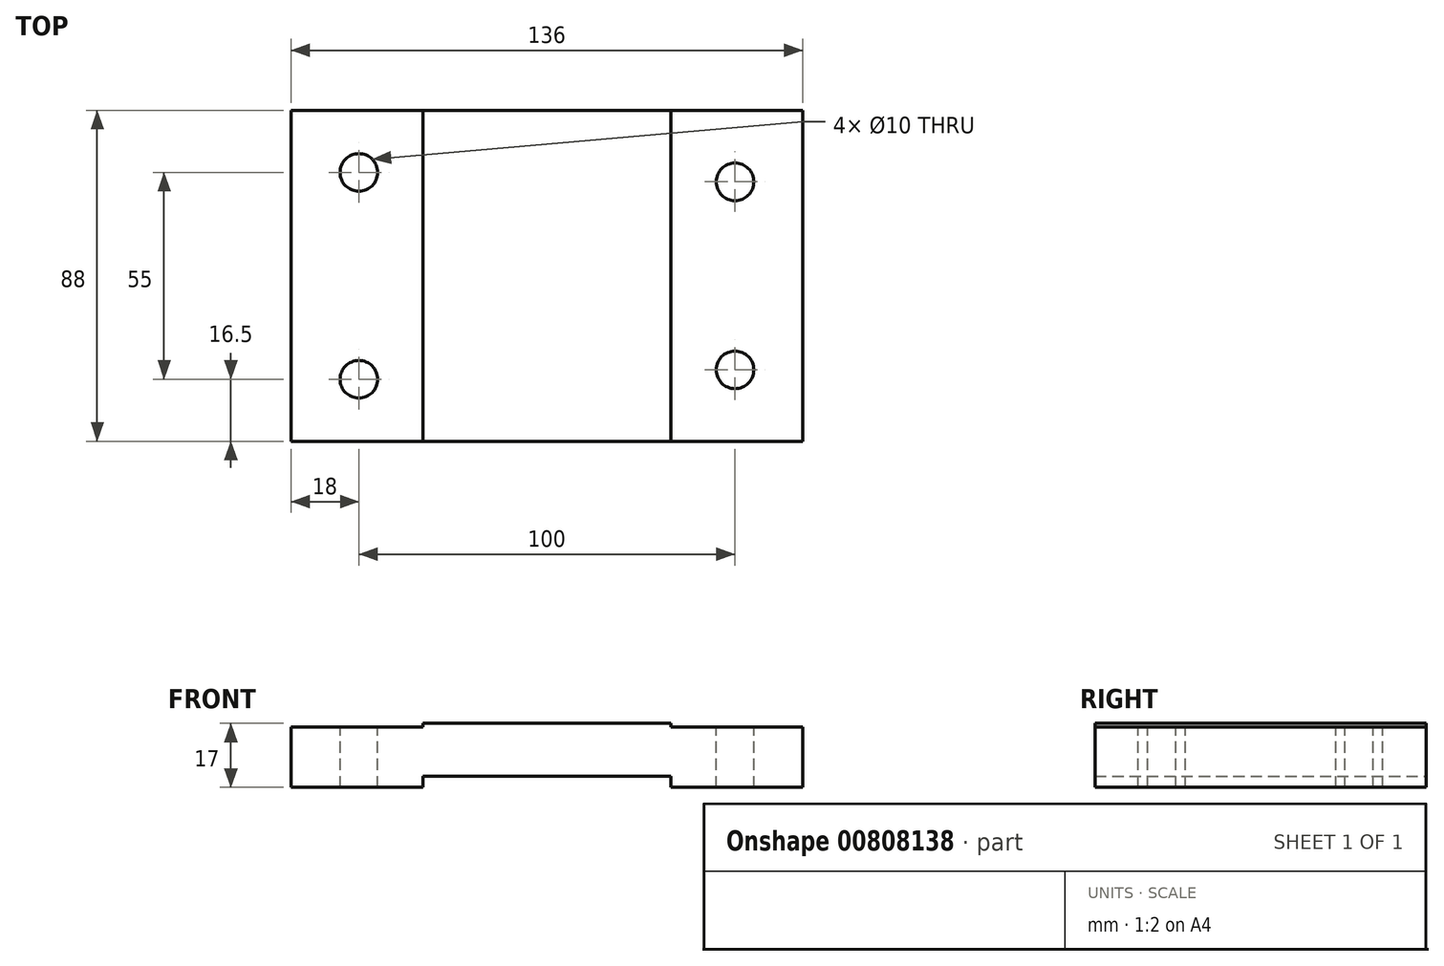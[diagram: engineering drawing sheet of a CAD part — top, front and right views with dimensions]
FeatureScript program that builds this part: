
annotation { "Feature Type Name" : "Feature", "Feature Type Description" : "" }
export const myFeature = defineFeature(function(context is Context, id is Id, definition is map)
    precondition{}
    {
        {
            var Q0;
            Q0=qCreatedBy(makeId("Front.planeOp"),FACE);
            var sketch = newSketch(context, id + "F0", { "sketchPlane" : qUnion([Q0])});
            skLineSegment(sketch, "E0.bottom", {"start": v(-33, 0) * mm, "end": v(-68, 0) * mm});
            skLineSegment(sketch, "E0.top", {"start": v(-33, 16) * mm, "end": v(-68, 16) * mm});
            skLineSegment(sketch, "E0.left", {"start": v(-33, 0) * mm, "end": v(-33, 16) * mm});
            skLineSegment(sketch, "E0.right", {"start": v(-68, 0) * mm, "end": v(-68, 16) * mm});
            skLineSegment(sketch, "E1.bottom", {"start": v(33, 0) * mm, "end": v(68, 0) * mm});
            skLineSegment(sketch, "E1.top", {"start": v(33, 16) * mm, "end": v(68, 16) * mm});
            skLineSegment(sketch, "E1.left", {"start": v(33, 0) * mm, "end": v(33, 16) * mm});
            skLineSegment(sketch, "E1.right", {"start": v(68, 0) * mm, "end": v(68, 16) * mm});
            skLineSegment(sketch, "E2.bottom", {"start": v(33, 3) * mm, "end": v(-33, 3) * mm});
            skLineSegment(sketch, "E2.top", {"start": v(33, 17) * mm, "end": v(-33, 17) * mm});
            skLineSegment(sketch, "E2.left", {"start": v(33, 3) * mm, "end": v(33, 17) * mm});
            skLineSegment(sketch, "E2.right", {"start": v(-33, 3) * mm, "end": v(-33, 17) * mm});
            skSolve(sketch);
        }
        {
            var Q0;
            Q0=makeQuery(id+"F0.imprint","IMPRINT",FACE,{"disambiguationData":[TD([[makeQuery(id+"F0.imprint","IMPRINT",EDGE,{"derivedFrom":sQuery(id+"F0.wireOp",EDGE,"E0.bottom")}),-1.0]])]});
            var Q1;
            {var subQ3=sQuery(id+"F0.wireOp",EDGE,"E2.bottom");Q1=makeQuery(id+"F0.imprint","IMPRINT",FACE,{"disambiguationData":[TD([[makeQuery(id+"F0.imprint","IMPRINT",EDGE,{"derivedFrom":subQ3}),-1.0]])]});}
            var Q2;
            Q2=makeQuery(id+"F0.imprint","IMPRINT",FACE,{"disambiguationData":[TD([[makeQuery(id+"F0.imprint","IMPRINT",EDGE,{"derivedFrom":sQuery(id+"F0.wireOp",EDGE,"E1.bottom")}),1.0]])]});
            extrude(context, id + "F1", {"entities" : qUnion([Q0, Q1, Q2]), "endBound" : BoundingType.SYMMETRIC, "depth" : 88 * mm, "offsetDistance" : 25 * mm});
        }
        {
            var Q0;
            Q0=makeQuery(id+"F1.opExtrude","SWEPT_FACE",FACE,{"disambiguationData":[OSD([sQuery(id+"F0.wireOp",EDGE,"E1.top")])]});
            cPlane(context, id + "F2", {"entities" : qUnion([Q0]), "cplaneType" : CPlaneType.OFFSET, "offset" : 0 * mm, "width" : 150 * mm, "height" : 150 * mm});
        }
        {
            var Q0;
            Q0=qCreatedBy(id+"F2.planeOp",FACE);
            var sketch = newSketch(context, id + "F3", { "sketchPlane" : qUnion([Q0])});
            skLineSegment(sketch, "E3", {"start": v(0, 0) * mm, "end": v(50, 0) * mm});
            skLineSegment(sketch, "E4", {"start": v(50, 0) * mm, "end": v(50, -25) * mm});
            skLineSegment(sketch, "E5", {"start": v(50, -25) * mm, "end": v(50, 25) * mm});
            skCircle(sketch, "E6", {"center": v(50, 25) * mm, "radius": 5 * mm});
            skCircle(sketch, "E7", {"center": v(50, -25) * mm, "radius": 5 * mm});
            skSolve(sketch);
        }
        {
            var Q0;
            Q0=makeQuery(id+"F1.opExtrude","SWEPT_FACE",FACE,{"disambiguationData":[OSD([sQuery(id+"F0.wireOp",EDGE,"E0.top")])]});
            var sketch = newSketch(context, id + "F4", { "sketchPlane" : qUnion([Q0])});
            skLineSegment(sketch, "E8", {"start": v(0, 0) * mm, "end": v(-50, 0) * mm});
            skLineSegment(sketch, "E9", {"start": v(-50, 27.5) * mm, "end": v(-50, -27.5) * mm});
            skCircle(sketch, "E10", {"center": v(-50, 27.5) * mm, "radius": 5 * mm});
            skCircle(sketch, "E11", {"center": v(-50, -27.5) * mm, "radius": 5 * mm});
            skSolve(sketch);
        }
        {
            var Q0;
            Q0=makeQuery(id+"F3.imprint","IMPRINT",FACE,{"disambiguationData":[TD([[makeQuery(id+"F3.imprint","IMPRINT",EDGE,{"derivedFrom":sQuery(id+"F3.wireOp",EDGE,"E6")}),1.0]])]});
            var Q1;
            Q1=makeQuery(id+"F3.imprint","IMPRINT",FACE,{"disambiguationData":[TD([[makeQuery(id+"F3.imprint","IMPRINT",EDGE,{"derivedFrom":sQuery(id+"F3.wireOp",EDGE,"E7")}),1.0]])]});
            extrude(context, id + "F5", {"entities" : qUnion([Q0, Q1]), "operationType" : NewBodyOperationType.REMOVE, "oppositeDirection" : true, "depth" : 25 * mm, "offsetDistance" : 25 * mm});
        }
        {
            var Q0;
            Q0=makeQuery(id+"F4.imprint","IMPRINT",FACE,{"disambiguationData":[TD([[makeQuery(id+"F4.imprint","IMPRINT",EDGE,{"derivedFrom":sQuery(id+"F4.wireOp",EDGE,"E11")}),1.0]])]});
            var Q1;
            Q1=makeQuery(id+"F4.imprint","IMPRINT",FACE,{"disambiguationData":[TD([[makeQuery(id+"F4.imprint","IMPRINT",EDGE,{"derivedFrom":sQuery(id+"F4.wireOp",EDGE,"E10")}),1.0]])]});
            extrude(context, id + "F6", {"entities" : qUnion([Q0, Q1]), "operationType" : NewBodyOperationType.REMOVE, "oppositeDirection" : true, "depth" : 25 * mm, "offsetDistance" : 25 * mm});
        }
    });
